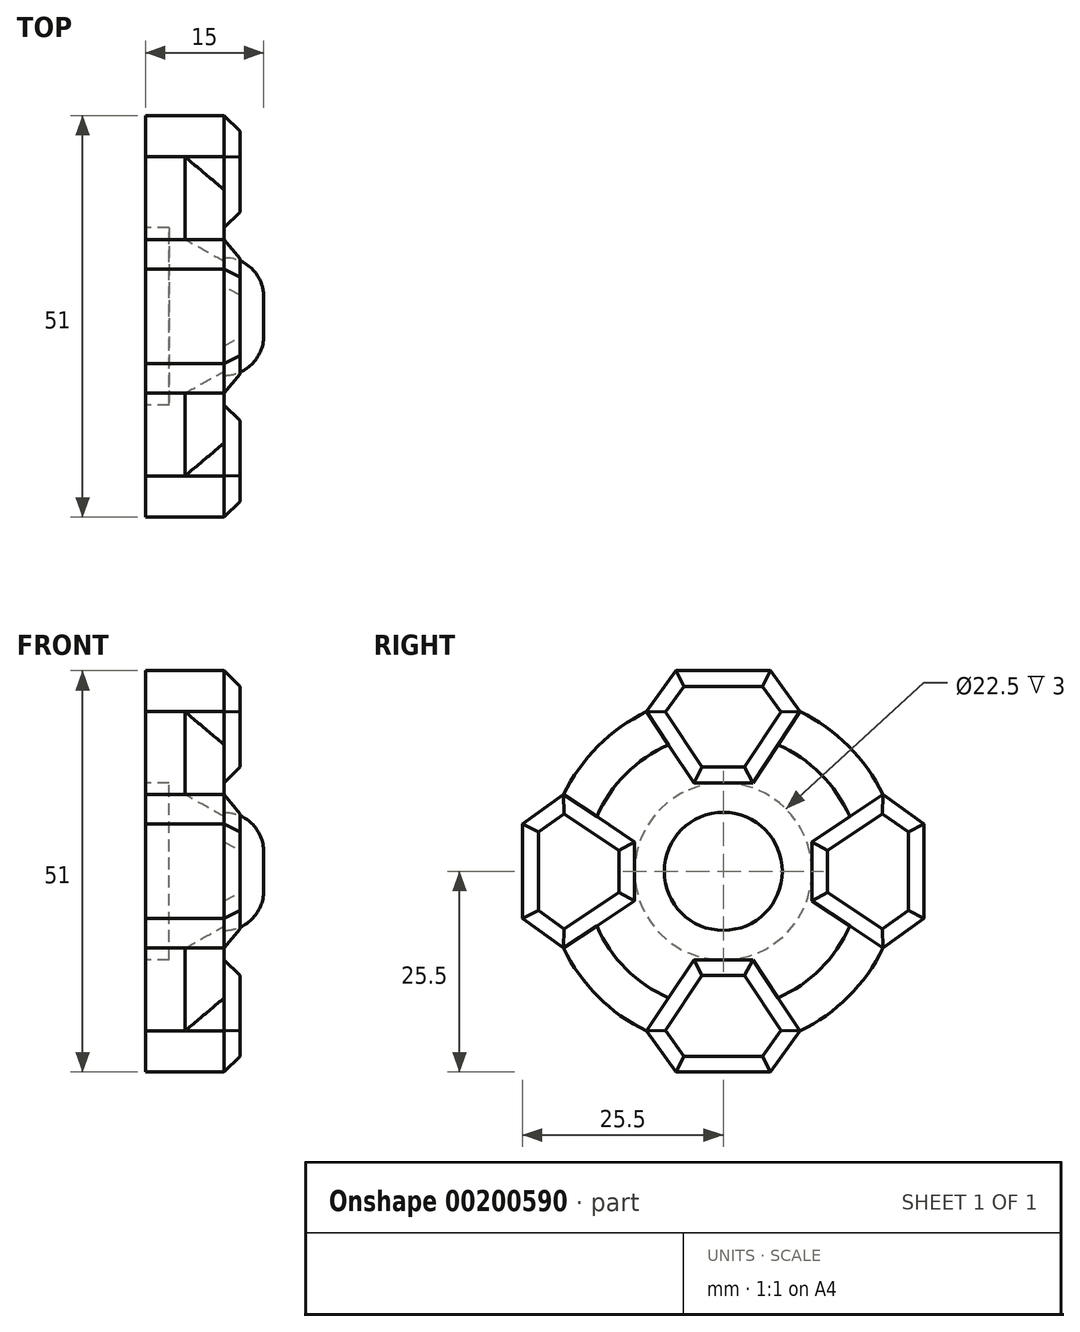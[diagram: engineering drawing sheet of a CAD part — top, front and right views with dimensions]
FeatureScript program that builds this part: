
annotation { "Feature Type Name" : "Feature", "Feature Type Description" : "" }
export const myFeature = defineFeature(function(context is Context, id is Id, definition is map)
    precondition{}
    {
        {
            var Q0;
            Q0=qCreatedBy(makeId("Right.planeOp"),FACE);
            var sketch = newSketch(context, id + "F0", { "sketchPlane" : qUnion([Q0])});
            skCircle(sketch, "E0", {"center": v(0, 0) * mm, "radius": 22.5 * mm});
            skLineSegment(sketch, "E1", {"start": v(0, 0) * mm, "end": v(0, 22.5) * mm, "construction": true});
            skLineSegment(sketch, "E2", {"start": v(0, 25.5) * mm, "end": v(-6, 25.5) * mm});
            skLineSegment(sketch, "E3", {"start": v(-6, 25.5) * mm, "end": v(-9.75, 20.28) * mm});
            skLineSegment(sketch, "E4", {"start": v(-9.75, 20.28) * mm, "end": v(-3.75, 11.25) * mm});
            skLineSegment(sketch, "E5", {"start": v(-3.75, 11.25) * mm, "end": v(0, 11.25) * mm});
            skLineSegment(sketch, "E6.MirrorCS", {"start": v(0, 25.5) * mm, "end": v(6, 25.5) * mm});
            skLineSegment(sketch, "E7.MirrorCS", {"start": v(6, 25.5) * mm, "end": v(9.75, 20.28) * mm});
            skLineSegment(sketch, "E8.MirrorCS", {"start": v(9.75, 20.28) * mm, "end": v(3.75, 11.25) * mm});
            skLineSegment(sketch, "E9.MirrorCS", {"start": v(3.75, 11.25) * mm, "end": v(0, 11.25) * mm});
            skPoint(sketch, "E10.center", {"position": v(-3.75, -3.75) * mm});
            skLineSegment(sketch, "E11.1.0", {"start": v(-25.5, 0) * mm, "end": v(-25.5, -6) * mm});
            skLineSegment(sketch, "E11.1.1", {"start": v(-25.5, 0) * mm, "end": v(-25.5, 6) * mm});
            skLineSegment(sketch, "E11.1.2", {"start": v(-25.5, 6) * mm, "end": v(-20.28, 9.75) * mm});
            skLineSegment(sketch, "E11.1.3", {"start": v(-25.5, -6) * mm, "end": v(-20.28, -9.75) * mm});
            skLineSegment(sketch, "E11.1.4", {"start": v(-20.28, -9.75) * mm, "end": v(-11.25, -3.75) * mm});
            skLineSegment(sketch, "E11.1.5", {"start": v(-11.25, -3.75) * mm, "end": v(-11.25, 0) * mm});
            skLineSegment(sketch, "E11.1.6", {"start": v(-11.25, 3.75) * mm, "end": v(-11.25, 0) * mm});
            skLineSegment(sketch, "E11.1.7", {"start": v(-20.28, 9.75) * mm, "end": v(-11.25, 3.75) * mm});
            skLineSegment(sketch, "E11.2.0", {"start": v(0, -25.5) * mm, "end": v(6, -25.5) * mm});
            skLineSegment(sketch, "E11.2.1", {"start": v(0, -25.5) * mm, "end": v(-6, -25.5) * mm});
            skLineSegment(sketch, "E11.2.2", {"start": v(-6, -25.5) * mm, "end": v(-9.75, -20.28) * mm});
            skLineSegment(sketch, "E11.2.3", {"start": v(6, -25.5) * mm, "end": v(9.75, -20.28) * mm});
            skLineSegment(sketch, "E11.2.4", {"start": v(9.75, -20.28) * mm, "end": v(3.75, -11.25) * mm});
            skLineSegment(sketch, "E11.2.5", {"start": v(3.75, -11.25) * mm, "end": v(0, -11.25) * mm});
            skLineSegment(sketch, "E11.2.6", {"start": v(-3.75, -11.25) * mm, "end": v(0, -11.25) * mm});
            skLineSegment(sketch, "E11.2.7", {"start": v(-9.75, -20.28) * mm, "end": v(-3.75, -11.25) * mm});
            skLineSegment(sketch, "E11.3.0", {"start": v(25.5, 0) * mm, "end": v(25.5, 6) * mm});
            skLineSegment(sketch, "E11.3.1", {"start": v(25.5, 0) * mm, "end": v(25.5, -6) * mm});
            skLineSegment(sketch, "E11.3.2", {"start": v(25.5, -6) * mm, "end": v(20.28, -9.75) * mm});
            skLineSegment(sketch, "E11.3.3", {"start": v(25.5, 6) * mm, "end": v(20.28, 9.75) * mm});
            skLineSegment(sketch, "E11.3.4", {"start": v(20.28, 9.75) * mm, "end": v(11.25, 3.75) * mm});
            skLineSegment(sketch, "E11.3.5", {"start": v(11.25, 3.75) * mm, "end": v(11.25, 0) * mm});
            skLineSegment(sketch, "E11.3.6", {"start": v(11.25, -3.75) * mm, "end": v(11.25, 0) * mm});
            skLineSegment(sketch, "E11.3.7", {"start": v(20.28, -9.75) * mm, "end": v(11.25, -3.75) * mm});
            skSolve(sketch);
        }
        {
            var Q0;
            {var subQ2=sQuery(id+"F0.wireOp",EDGE,"E4");Q0=makeQuery(id+"F0.imprint","IMPRINT",FACE,{"disambiguationData":[TD([[makeQuery(id+"F0.imprint","IMPRINT",EDGE,{"derivedFrom":subQ2}),-1.0]])]});}
            extrude(context, id + "F1", {"entities" : qUnion([Q0]), "depth" : 10 * mm});
        }
        {
            var Q0;
            {var subQ1=sQuery(id+"F0.wireOp",EDGE,"E4");Q0=makeQuery(id+"F0.imprint","IMPRINT",FACE,{"disambiguationData":[TD([[makeQuery(id+"F0.imprint","IMPRINT",EDGE,{"derivedFrom":subQ1}),1.0]])]});}
            var Q1;
            Q1=makeQuery(id+"F0.imprint","IMPRINT",FACE,{"disambiguationData":[TD([[makeQuery(id+"F0.imprint","IMPRINT",EDGE,{"derivedFrom":sQuery(id+"F0.wireOp",EDGE,"E2")}),1.0]])]});
            var Q2;
            {var subQ1=sQuery(id+"F0.wireOp",EDGE,"E11.1.4");Q2=makeQuery(id+"F0.imprint","IMPRINT",FACE,{"disambiguationData":[TD([[makeQuery(id+"F0.imprint","IMPRINT",EDGE,{"derivedFrom":subQ1}),1.0]])]});}
            var Q3;
            Q3=makeQuery(id+"F0.imprint","IMPRINT",FACE,{"disambiguationData":[TD([[makeQuery(id+"F0.imprint","IMPRINT",EDGE,{"derivedFrom":sQuery(id+"F0.wireOp",EDGE,"E11.1.0")}),1.0]])]});
            var Q4;
            {var subQ0=sQuery(id+"F0.wireOp",EDGE,"E11.2.4");Q4=makeQuery(id+"F0.imprint","IMPRINT",FACE,{"disambiguationData":[TD([[makeQuery(id+"F0.imprint","IMPRINT",EDGE,{"derivedFrom":subQ0}),1.0]])]});}
            var Q5;
            Q5=makeQuery(id+"F0.imprint","IMPRINT",FACE,{"disambiguationData":[TD([[makeQuery(id+"F0.imprint","IMPRINT",EDGE,{"derivedFrom":sQuery(id+"F0.wireOp",EDGE,"E11.2.0")}),1.0]])]});
            var Q6;
            {var subQ0=sQuery(id+"F0.wireOp",EDGE,"E11.3.4");Q6=makeQuery(id+"F0.imprint","IMPRINT",FACE,{"disambiguationData":[TD([[makeQuery(id+"F0.imprint","IMPRINT",EDGE,{"derivedFrom":subQ0}),1.0]])]});}
            var Q7;
            Q7=makeQuery(id+"F0.imprint","IMPRINT",FACE,{"disambiguationData":[TD([[makeQuery(id+"F0.imprint","IMPRINT",EDGE,{"derivedFrom":sQuery(id+"F0.wireOp",EDGE,"E11.3.0")}),1.0]])]});
            extrude(context, id + "F2", {"entities" : qUnion([Q0, Q1, Q2, Q3, Q4, Q5, Q6, Q7]), "operationType" : NewBodyOperationType.ADD, "depth" : 12 * mm});
        }
        {
            var Q0;
            {var subQ0=sQuery(id+"F0.wireOp",EDGE,"E0");Q0=makeQuery(id+"F1.opExtrude","CAP_EDGE",EDGE,{"disambiguationData":[OSD([subQ0]),TDD([makeQuery(id+"F0.imprint","IMPRINT",EDGE,{"disambiguationData":[TD([[makeQuery(id+"F0.imprint","INTERSECT",VERTEX,{"derivedFrom":[subQ0,sQuery(id+"F0.wireOp",EDGE,"E7.MirrorCS"),sQuery(id+"F0.wireOp",EDGE,"E8.MirrorCS")]}),1.0]])],"derivedFrom":subQ0})])],"isStart":false});}
            var Q1;
            {var subQ0=sQuery(id+"F0.wireOp",EDGE,"E0");Q1=makeQuery(id+"F1.opExtrude","CAP_EDGE",EDGE,{"disambiguationData":[OSD([subQ0]),TDD([makeQuery(id+"F0.imprint","IMPRINT",EDGE,{"disambiguationData":[TD([[makeQuery(id+"F0.imprint","INTERSECT",VERTEX,{"derivedFrom":[subQ0,sQuery(id+"F0.wireOp",EDGE,"E3"),sQuery(id+"F0.wireOp",EDGE,"E4")]}),-1.0]])],"derivedFrom":subQ0})])],"isStart":false});}
            var Q2;
            {var subQ0=sQuery(id+"F0.wireOp",EDGE,"E0");Q2=makeQuery(id+"F1.opExtrude","CAP_EDGE",EDGE,{"disambiguationData":[OSD([subQ0]),TDD([makeQuery(id+"F0.imprint","IMPRINT",EDGE,{"disambiguationData":[TD([[makeQuery(id+"F0.imprint","INTERSECT",VERTEX,{"derivedFrom":[subQ0,sQuery(id+"F0.wireOp",EDGE,"E10.1.3"),sQuery(id+"F0.wireOp",EDGE,"E10.1.4")]}),-1.0]])],"derivedFrom":subQ0})])],"isStart":false});}
            var Q3;
            {var subQ0=sQuery(id+"F0.wireOp",EDGE,"E0");Q3=makeQuery(id+"F1.opExtrude","CAP_EDGE",EDGE,{"disambiguationData":[OSD([subQ0]),TDD([makeQuery(id+"F0.imprint","IMPRINT",EDGE,{"disambiguationData":[TD([[makeQuery(id+"F0.imprint","INTERSECT",VERTEX,{"derivedFrom":[subQ0,sQuery(id+"F0.wireOp",EDGE,"E10.2.3"),sQuery(id+"F0.wireOp",EDGE,"E10.2.4")]}),-1.0]])],"derivedFrom":subQ0})])],"isStart":false});}
            chamfer(context, id + "F3", {"entities" : qUnion([Q0, Q1, Q2, Q3]), "width" : 5 * mm, "tangentPropagation" : true});
        }
        {
            var Q0;
            Q0=makeQuery(id+"F2.opExtrude","CAP_EDGE",EDGE,{"disambiguationData":[OSD([sQuery(id+"F0.wireOp",EDGE,"E2"),sQuery(id+"F0.wireOp",EDGE,"E6.MirrorCS")])],"isStart":false});
            var Q1;
            Q1=makeQuery(id+"F2.opExtrude","CAP_EDGE",EDGE,{"disambiguationData":[OSD([sQuery(id+"F0.wireOp",EDGE,"E3")])],"isStart":false});
            var Q2;
            Q2=makeQuery(id+"F2.opExtrude","CAP_EDGE",EDGE,{"disambiguationData":[OSD([sQuery(id+"F0.wireOp",EDGE,"E7.MirrorCS")])],"isStart":false});
            var Q3;
            Q3=makeQuery(id+"F2.opExtrude","CAP_EDGE",EDGE,{"disambiguationData":[OSD([sQuery(id+"F0.wireOp",EDGE,"E4")])],"isStart":false});
            var Q4;
            Q4=makeQuery(id+"F2.opExtrude","CAP_EDGE",EDGE,{"disambiguationData":[OSD([sQuery(id+"F0.wireOp",EDGE,"E8.MirrorCS")])],"isStart":false});
            var Q5;
            Q5=makeQuery(id+"F2.opExtrude","CAP_EDGE",EDGE,{"disambiguationData":[OSD([sQuery(id+"F0.wireOp",EDGE,"E5"),sQuery(id+"F0.wireOp",EDGE,"E9.MirrorCS")])],"isStart":false});
            var Q6;
            Q6=makeQuery(id+"F2.opExtrude","CAP_EDGE",EDGE,{"disambiguationData":[OSD([sQuery(id+"F0.wireOp",EDGE,"E11.1.7")])],"isStart":false});
            var Q7;
            Q7=makeQuery(id+"F2.opExtrude","CAP_EDGE",EDGE,{"disambiguationData":[OSD([sQuery(id+"F0.wireOp",EDGE,"E11.1.2")])],"isStart":false});
            var Q8;
            Q8=makeQuery(id+"F2.opExtrude","CAP_EDGE",EDGE,{"disambiguationData":[OSD([sQuery(id+"F0.wireOp",EDGE,"E11.1.0"),sQuery(id+"F0.wireOp",EDGE,"E11.1.1")])],"isStart":false});
            var Q9;
            Q9=makeQuery(id+"F2.opExtrude","CAP_EDGE",EDGE,{"disambiguationData":[OSD([sQuery(id+"F0.wireOp",EDGE,"E11.1.3")])],"isStart":false});
            var Q10;
            Q10=makeQuery(id+"F2.opExtrude","CAP_EDGE",EDGE,{"disambiguationData":[OSD([sQuery(id+"F0.wireOp",EDGE,"E11.1.4")])],"isStart":false});
            var Q11;
            Q11=makeQuery(id+"F2.opExtrude","CAP_EDGE",EDGE,{"disambiguationData":[OSD([sQuery(id+"F0.wireOp",EDGE,"E11.1.5"),sQuery(id+"F0.wireOp",EDGE,"E11.1.6")])],"isStart":false});
            var Q12;
            Q12=makeQuery(id+"F2.opExtrude","CAP_EDGE",EDGE,{"disambiguationData":[OSD([sQuery(id+"F0.wireOp",EDGE,"E11.2.5"),sQuery(id+"F0.wireOp",EDGE,"E11.2.6")])],"isStart":false});
            var Q13;
            Q13=makeQuery(id+"F2.opExtrude","CAP_EDGE",EDGE,{"disambiguationData":[OSD([sQuery(id+"F0.wireOp",EDGE,"E11.2.7")])],"isStart":false});
            var Q14;
            Q14=makeQuery(id+"F2.opExtrude","CAP_EDGE",EDGE,{"disambiguationData":[OSD([sQuery(id+"F0.wireOp",EDGE,"E11.2.2")])],"isStart":false});
            var Q15;
            Q15=makeQuery(id+"F2.opExtrude","CAP_FACE",FACE,{"disambiguationData":[OSD([sQuery(id+"F0.wireOp",EDGE,"E11.2.0"),sQuery(id+"F0.wireOp",EDGE,"E11.2.1"),sQuery(id+"F0.wireOp",EDGE,"E11.2.2"),sQuery(id+"F0.wireOp",EDGE,"E11.2.3"),sQuery(id+"F0.wireOp",EDGE,"E11.2.4"),sQuery(id+"F0.wireOp",EDGE,"E11.2.5"),sQuery(id+"F0.wireOp",EDGE,"E11.2.6"),sQuery(id+"F0.wireOp",EDGE,"E11.2.7")])],"isStart":false});
            var Q16;
            Q16=makeQuery(id+"F2.opExtrude","CAP_EDGE",EDGE,{"disambiguationData":[OSD([sQuery(id+"F0.wireOp",EDGE,"E11.3.7")])],"isStart":false});
            var Q17;
            Q17=makeQuery(id+"F2.opExtrude","CAP_EDGE",EDGE,{"disambiguationData":[OSD([sQuery(id+"F0.wireOp",EDGE,"E11.3.5"),sQuery(id+"F0.wireOp",EDGE,"E11.3.6")])],"isStart":false});
            var Q18;
            Q18=makeQuery(id+"F2.opExtrude","CAP_EDGE",EDGE,{"disambiguationData":[OSD([sQuery(id+"F0.wireOp",EDGE,"E11.3.4")])],"isStart":false});
            var Q19;
            Q19=makeQuery(id+"F2.opExtrude","CAP_EDGE",EDGE,{"disambiguationData":[OSD([sQuery(id+"F0.wireOp",EDGE,"E11.3.3")])],"isStart":false});
            var Q20;
            Q20=makeQuery(id+"F2.opExtrude","CAP_EDGE",EDGE,{"disambiguationData":[OSD([sQuery(id+"F0.wireOp",EDGE,"E11.3.0"),sQuery(id+"F0.wireOp",EDGE,"E11.3.1")])],"isStart":false});
            var Q21;
            Q21=makeQuery(id+"F2.opExtrude","CAP_EDGE",EDGE,{"disambiguationData":[OSD([sQuery(id+"F0.wireOp",EDGE,"E11.3.2")])],"isStart":false});
            chamfer(context, id + "F4", {"entities" : qUnion([Q0, Q1, Q2, Q3, Q4, Q5, Q6, Q7, Q8, Q9, Q10, Q11, Q12, Q13, Q14, Q15, Q16, Q17, Q18, Q19, Q20, Q21]), "width" : 2 * mm, "tangentPropagation" : true});
        }
        {
            var Q0;
            Q0=makeQuery(id+"F1.opExtrude","CAP_FACE",FACE,{"disambiguationData":[OSD([sQuery(id+"F0.wireOp",EDGE,"E0"),sQuery(id+"F0.wireOp",EDGE,"E4"),sQuery(id+"F0.wireOp",EDGE,"E5"),sQuery(id+"F0.wireOp",EDGE,"E8.MirrorCS"),sQuery(id+"F0.wireOp",EDGE,"E9.MirrorCS"),sQuery(id+"F0.wireOp",EDGE,"E10.1.4"),sQuery(id+"F0.wireOp",EDGE,"E10.1.5"),sQuery(id+"F0.wireOp",EDGE,"E10.1.6"),sQuery(id+"F0.wireOp",EDGE,"E10.1.7"),sQuery(id+"F0.wireOp",EDGE,"E10.2.4"),sQuery(id+"F0.wireOp",EDGE,"E10.2.5"),sQuery(id+"F0.wireOp",EDGE,"E10.2.6"),sQuery(id+"F0.wireOp",EDGE,"E10.2.7"),sQuery(id+"F0.wireOp",EDGE,"E10.3.4"),sQuery(id+"F0.wireOp",EDGE,"E10.3.5"),sQuery(id+"F0.wireOp",EDGE,"E10.3.6"),sQuery(id+"F0.wireOp",EDGE,"E10.3.7")])],"isStart":false});
            var sketch = newSketch(context, id + "F5", { "sketchPlane" : qUnion([Q0])});
            skCircle(sketch, "E12", {"center": v(0, 0) * mm, "radius": 7.5 * mm});
            skSolve(sketch);
        }
        {
            var Q0;
            Q0=makeQuery(id+"F5.imprint","IMPRINT",FACE,{"disambiguationData":[TD([[makeQuery(id+"F5.imprint","IMPRINT",EDGE,{"derivedFrom":sQuery(id+"F5.wireOp",EDGE,"E12")}),1.0]])]});
            extrude(context, id + "F6", {"entities" : qUnion([Q0]), "depth" : 5 * mm});
        }
        {
            var Q0;
            Q0=makeQuery(id+"F6.opExtrude","CAP_EDGE",EDGE,{"disambiguationData":[OSD([sQuery(id+"F5.wireOp",EDGE,"E12")])],"isStart":false});
            fillet(context, id + "F7", {"entities" : qUnion([Q0]), "radius" : 5 * mm, "tangentPropagation" : true, "allowEdgeOverflow" : false});
        }
        {
            var Q0;
            {var subQ2=sQuery(id+"F0.wireOp",EDGE,"E4");Q0=makeQuery(id+"F0.imprint","IMPRINT",FACE,{"disambiguationData":[TD([[makeQuery(id+"F0.imprint","IMPRINT",EDGE,{"derivedFrom":subQ2}),-1.0]])]});}
            var sketch = newSketch(context, id + "F8", { "sketchPlane" : qUnion([Q0])});
            skCircle(sketch, "E13", {"center": v(0, 0) * mm, "radius": 11.25 * mm});
            skSolve(sketch);
        }
        {
            var Q0;
            {var subQ0=sQuery(id+"F8.wireOp",EDGE,"E13");var subQ1=makeQuery(id+"F8.imprint","INTERSECT",VERTEX,{"derivedFrom":[makeQuery(id+"F0.imprint","IMPRINT",EDGE,{"derivedFrom":sQuery(id+"F0.wireOp",EDGE,"E5")}),makeQuery(id+"F0.imprint","IMPRINT",EDGE,{"derivedFrom":sQuery(id+"F0.wireOp",EDGE,"E9.MirrorCS")}),subQ0]});Q0=makeQuery(id+"F8.imprint","IMPRINT",FACE,{"disambiguationData":[TD([[makeQuery(id+"F8.imprint","IMPRINT",EDGE,{"disambiguationData":[TD([[subQ1,1.0]])],"derivedFrom":subQ0}),1.0]])]});}
            extrude(context, id + "F9", {"entities" : qUnion([Q0]), "operationType" : NewBodyOperationType.REMOVE, "depth" : 3 * mm});
        }
    });
